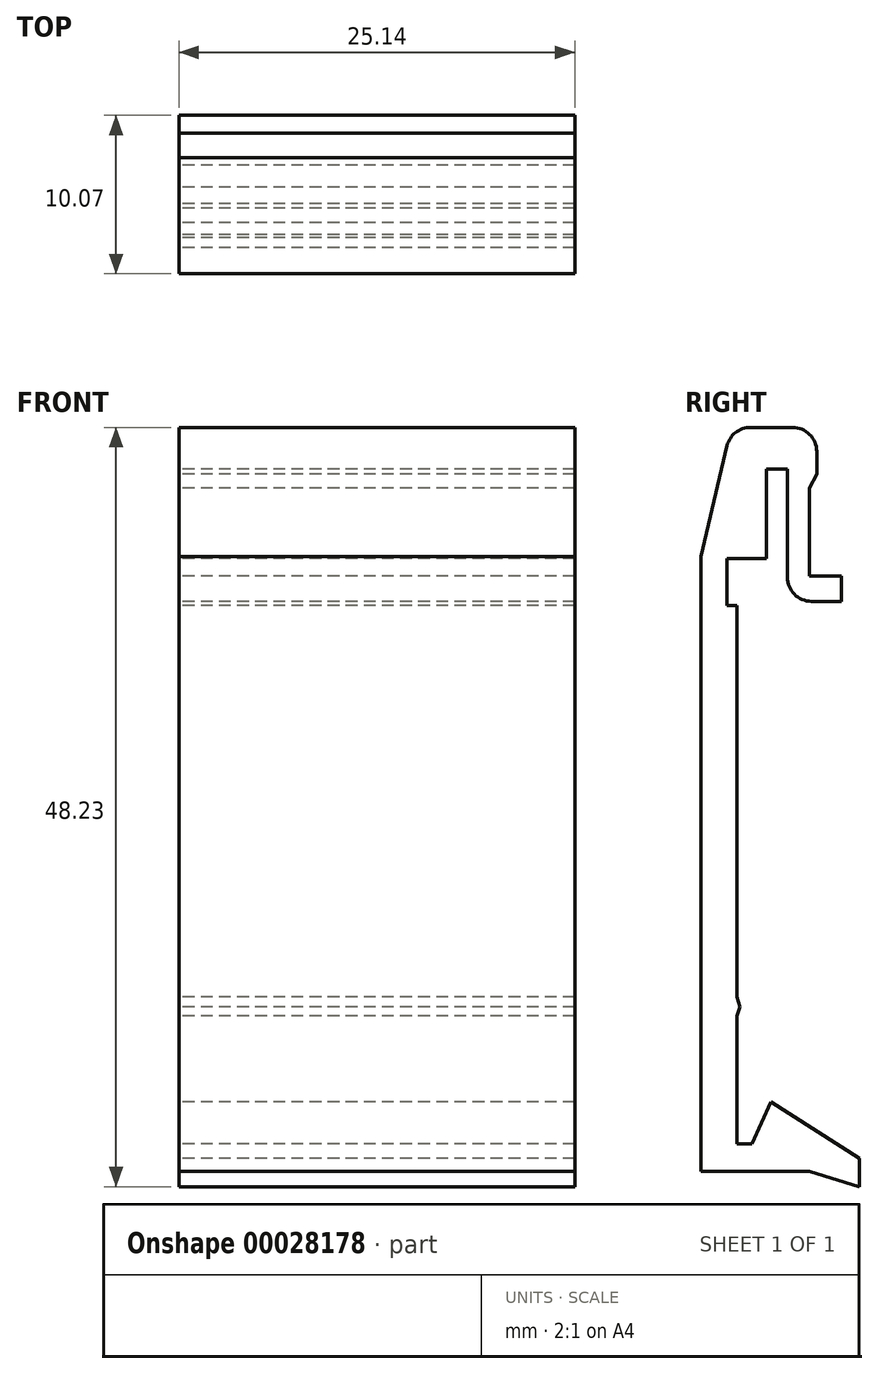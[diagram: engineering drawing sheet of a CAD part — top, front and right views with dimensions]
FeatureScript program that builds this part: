
annotation { "Feature Type Name" : "Feature", "Feature Type Description" : "" }
export const myFeature = defineFeature(function(context is Context, id is Id, definition is map)
    precondition{}
    {
        {
            var Q0;
            Q0=qCreatedBy(makeId("Right.planeOp"),FACE);
            var sketch = newSketch(context, id + "F0", { "sketchPlane" : qUnion([Q0])});
            skLineSegment(sketch, "E0.5", {"start": v(6.91, 23.86) * mm, "end": v(6.91, 18.29) * mm});
            skLineSegment(sketch, "E0.12", {"start": v(4.18, 25.06) * mm, "end": v(4.18, 19.4) * mm});
            skLineSegment(sketch, "E0.11", {"start": v(1.68, 26.55) * mm, "end": v(0, 19.52) * mm});
            skLineSegment(sketch, "E0.20", {"start": v(2.29, -9.68) * mm, "end": v(2.29, -17.8) * mm});
            skLineSegment(sketch, "E0.0", {"start": v(2.29, 16.4) * mm, "end": v(2.29, -8.45) * mm});
            skLineSegment(sketch, "E0.18", {"start": v(2.29, -9.68) * mm, "end": v(2.5, -9.1) * mm});
            skLineSegment(sketch, "E0.16", {"start": v(1.68, 19.4) * mm, "end": v(1.68, 16.4) * mm});
            skArc(sketch, "E0.8", {"start": v(7.37, 26.2) * mm, "mid": v(6.92, 27.27) * mm, "end": v(5.84, 27.72) * mm});
            skLineSegment(sketch, "E0.22", {"start": v(4.45, -15.14) * mm, "end": v(3.27, -17.8) * mm});
            skLineSegment(sketch, "E0.23", {"start": v(10.07, -18.71) * mm, "end": v(4.45, -15.14) * mm});
            skLineSegment(sketch, "E0.14", {"start": v(5.5, 18.2) * mm, "end": v(5.5, 25.06) * mm});
            skLineSegment(sketch, "E0.25", {"start": v(6.91, -19.52) * mm, "end": v(10.07, -20.51) * mm});
            skLineSegment(sketch, "E0.17", {"start": v(1.68, 16.4) * mm, "end": v(2.29, 16.4) * mm});
            skLineSegment(sketch, "E0.19", {"start": v(2.5, -9.1) * mm, "end": v(2.29, -8.45) * mm});
            skLineSegment(sketch, "E0.21", {"start": v(2.29, -17.8) * mm, "end": v(3.27, -17.8) * mm});
            skLineSegment(sketch, "E0.24", {"start": v(10.07, -18.71) * mm, "end": v(10.07, -20.51) * mm});
            skLineSegment(sketch, "E0.26", {"start": v(6.91, -19.52) * mm, "end": v(0, -19.52) * mm});
            skLineSegment(sketch, "E0.4", {"start": v(6.91, 18.29) * mm, "end": v(8.94, 18.29) * mm});
            skLineSegment(sketch, "E0.6", {"start": v(6.91, 23.86) * mm, "end": v(7.37, 24.77) * mm});
            skLineSegment(sketch, "E0.7", {"start": v(7.37, 26.2) * mm, "end": v(7.37, 24.77) * mm});
            skLineSegment(sketch, "E0.3", {"start": v(8.94, 18.29) * mm, "end": v(8.94, 16.67) * mm});
            skArc(sketch, "E0.10", {"start": v(3.16, 27.72) * mm, "mid": v(2.21, 27.4) * mm, "end": v(1.68, 26.55) * mm});
            skLineSegment(sketch, "E0.9", {"start": v(3.16, 27.72) * mm, "end": v(5.84, 27.72) * mm});
            skArc(sketch, "E0.2", {"start": v(5.5, 18.2) * mm, "mid": v(5.95, 17.12) * mm, "end": v(7.03, 16.67) * mm});
            skLineSegment(sketch, "E0.1", {"start": v(8.94, 16.67) * mm, "end": v(7.03, 16.67) * mm});
            skLineSegment(sketch, "E0.15", {"start": v(4.18, 19.4) * mm, "end": v(1.68, 19.4) * mm});
            skLineSegment(sketch, "E0.13", {"start": v(5.5, 25.06) * mm, "end": v(4.18, 25.06) * mm});
            skLineSegment(sketch, "E1", {"start": v(0, 19.52) * mm, "end": v(0, -19.52) * mm});
            skSolve(sketch);
        }
        {
            var Q0;
            Q0=qSketchRegion(id+"F0",true);
            extrude(context, id + "F1", {"entities" : qUnion([Q0]), "endBound" : BoundingType.SYMMETRIC, "depth" : 25.15 * mm});
        }
    });
